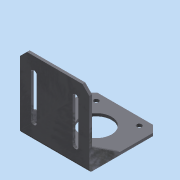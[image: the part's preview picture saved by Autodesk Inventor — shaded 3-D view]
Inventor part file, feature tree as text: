
AUTODESK INVENTOR PART (.ipt)
format: ipt  version: 2012 (Build 160160000, 160)  size: 161,792 bytes
history: native  units: mm
features: sketch x3, extrude x3, fillet x2, other x1, pattern_linear x1, hole x1
ambient origin geometry x8: Origin, YZ Plane, XZ Plane, XY Plane, X Axis, Y Axis, Z Axis, Center Point
feature tree (11):
  other  "Sólido1"
  sketch  "Boceto1"  dims[d0=50.0mm d1=51.0mm]
  extrude  "Extrusión1"  Depth=51.0mm
  extrude  "Extrusión2"  Depth=22.1mm
  extrude  "Extrusión3"  Depth=5.0mm
  pattern_linear  "Patrón rectangular1"  Spacing1=5.0mm  [1 undecoded]
  fillet  "Empalme1"  Radius=5.0mm
  fillet  "Empalme2"  Radius=2.0mm
  hole  "Hole1"  [1 undecoded]
  sketch  "Boceto2"  dims[d2=21.0mm d3=22.1mm]
  sketch  "Boceto3"  dims[d15=5.0mm d16=5.0mm d17=5.0mm d18=5.0mm d19=2.0mm d20=0.0mm d21=53.0mm d24=4.2mm d25=7.9mm d26=2.1mm d27=2.1mm d28=20.0mm d30=30.0mm d31=10.0mm d33=10.0mm d35=2.0mm d36=0.0mm d37=5.0mm d38=5.0mm d39=5.0mm d40=5.0mm d41=20.0mm d42=13.0mm d43=2.0mm d44=0.0mm d45=20.0mm d47=48.0mm d48=2.0mm d49=2.0mm d50=15.5mm d51=15.5mm d52=20.0mm d54=31.0mm d55=20.0mm d57=31.0mm d60=3.5mm d61=6.0mm d62=3.023mm d63=2.0mm d64=14.3117mm d65=8.0mm d66=20.594885mm d67=30.0mm d68=11.0mm]
note: 2 required parameter values undecoded (feature->parameter linkage not recoverable at this tier; creation-order binding heuristic only, values carry confidence <= 0.55)
